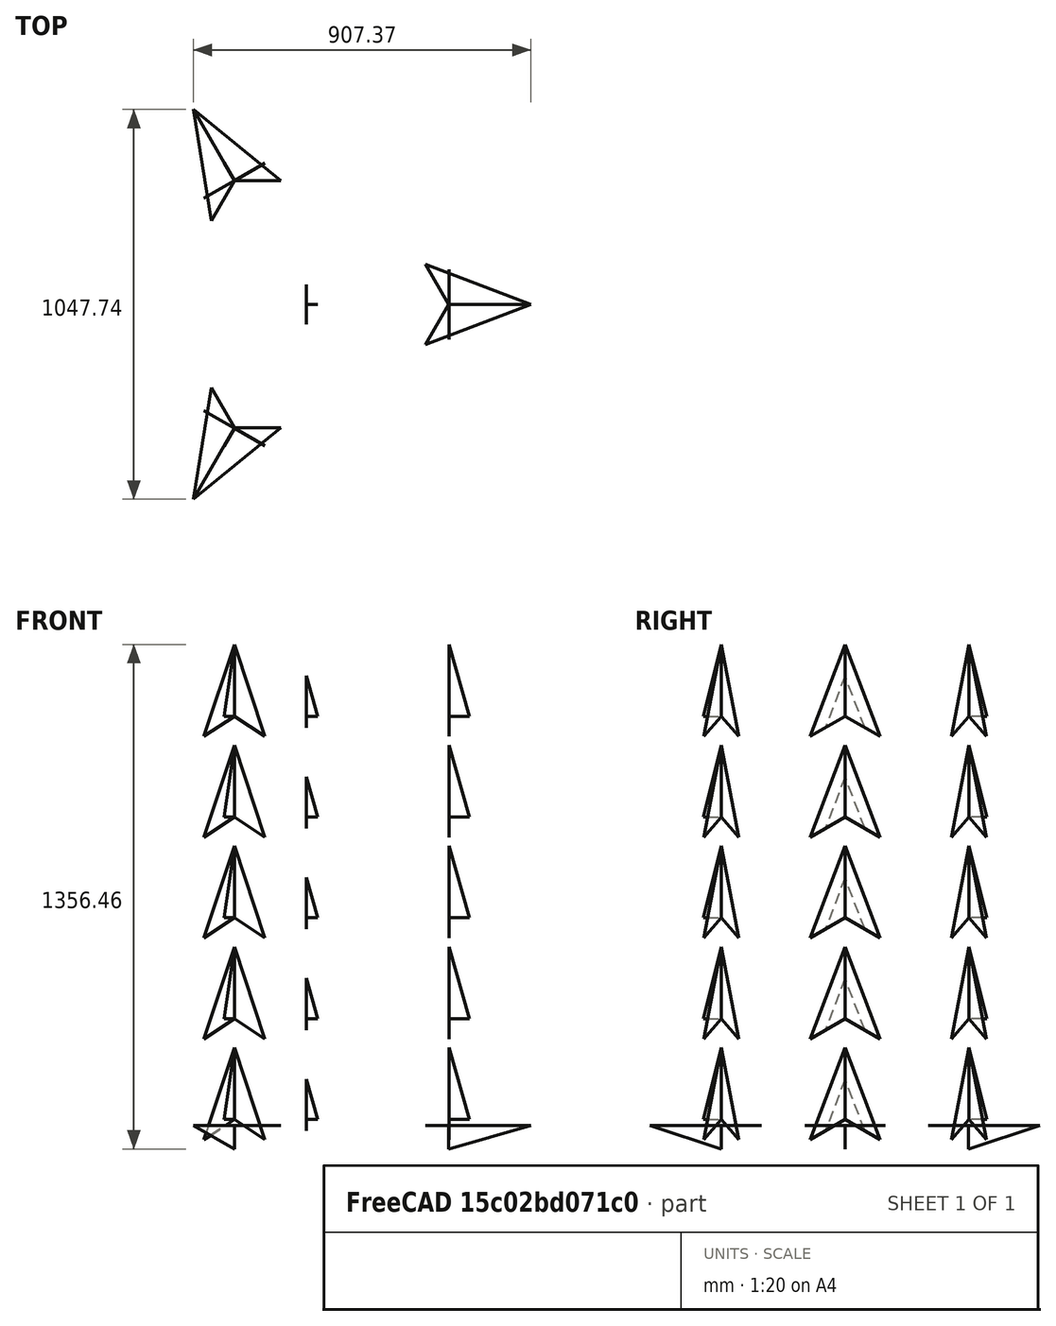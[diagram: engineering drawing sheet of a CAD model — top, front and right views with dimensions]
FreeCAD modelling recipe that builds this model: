
FCSTD DOCUMENT  (FreeCAD 1.1R38827 (Git))
Label: composit_stand3_plexiglass_outer_main
License: All rights reserved
LicenseURL: http://en.wikipedia.org/wiki/All_rights_reserved
objects: Part::FeaturePython×5, Sketcher::SketchObject×2, Part::Mirroring×2, App::Link×1, Part::Compound×1, Spreadsheet::Sheet×1
note: 12 computed .brp shape members not serialized (recipe doc carries the construction recipe); baked Part::Feature solids carry a one-line shape summary decoded from their .brp
EXTERNAL_REF file=composit_stand3_basement_bottom_main.FCStd obj=Placment
EXTERNAL_REF file=composit_stand3_bar_main.FCStd obj=Sketch

FEATURE [App::Link] Link  label="bar_placement"
  LinkTransform = true
  LinkedObject = -> <external composit_stand3_basement_bottom_main.FCStd>#Placment
FEATURE [Sketcher::SketchObject] Sketch001  label="base_Sketch_per"
  ArcFitTolerance = 0
  FullyConstrained = true
  MakeInternals = false
  expr: .Constraints.r = <<bar_placement>>.LinkedObject.Placement.Base.x
  expr: Constraints[2] = <<composit_stand3_bar_main>>#<<base_Sketch>>.Constraints.width - 8 mm
  sketch-geometry (1):
    g0: LineSegment StartX=383.5 StartY=-14.3 StartZ=0 EndX=383.5 EndY=14.3 EndZ=0
  constraints (3):
    c: Symmetric(g0,g0,g-1)
    c: DistanceX(g0) = 383.5  'r'
    c: DistanceY(g0,g0) = 28.6
FEATURE [Sketcher::SketchObject] Sketch  label="base_Sketch"
  ArcFitTolerance = 0
  ExternalGeometry = -> [Sketch001]
  FullyConstrained = false
  MakeInternals = false
  sketch-geometry (2):
    g0: ArcOfCircle CenterX=-17.9061 CenterY=-31.0143 CenterZ=0 NormalX=0 NormalY=0 NormalZ=1 AngleXU=0 Radius=403.956 StartAngle=0.112413 EndAngle=1.0472
    g1: LineSegment [constr] StartX=-17.9061 StartY=-31.0143 StartZ=0 EndX=184.072 EndY=318.822 EndZ=0
  constraints (6):
    c: Coincident(g1,g0)
    c: Coincident(g1,g0)
    c: Angle(g1) = 1.0472
    c: Coincident(g0,g-3)
    c: PointOnObject(g-1,g1)
    c: DistanceX(g-1,g-3) = 383.5  'offset'
FEATURE [Part::FeaturePython] PolarArray  # WARN: FeaturePython — macro-defined, semantics opaque (R4)
  Alignment = 0
  AttacherType = Attacher::AttachEngine3D
  CellStart = A1
  Count = 3
  DistributionLaw = 0
  EndInclusive = false
  ExposePlacement = false
  FlipX = false
  FlipZ = false
  GeneratorMode = 0
  MarkerShape = 1
  MarkerSize = 0
  NumElements = 3
  OrientMode = 2
  Radius = 383.5
  Reverse = false
  SpanEnd = 360
  SpanStart = 0
  Step = 120
  Type = lattice2PolarArray2.PolarArray
  UseArcRadius = false
  UseArcRange = 0
  VSGVersion = 1
  Values = 0.0 | 120.0 | 240.0
  ValuesSource = 2
  isLattice = 1
  expr: Radius = <<base_Sketch_per>>.Constraints.r
FEATURE [Part::FeaturePython] Populate  label="Populate PolarArray with base_Sketch_per"  # WARN: FeaturePython — macro-defined, semantics opaque (R4)
  Copying = 0
  ExposePlacement = false
  MarkerShape = 1
  MarkerSize = 0
  NumElements = 0
  Object = -> Sketch001
  OutputCompounding = 1
  PlacementsTo = -> PolarArray
  Referencing = 1
  Type = lattice2PopulateCopies.LatticePopulateCopies
  isLattice = 0
FEATURE [Part::Mirroring] Part__Mirroring  label="base_Sketch (Mirror #1)"
  Base = (0,0,0)
  Normal = (0.866025,-0.5,0)
  Source = -> Sketch
  expr: .Normal.x = sin(60)
  expr: .Normal.y = -cos(60)
FEATURE [Part::Compound] Compound
  Links = -> [Sketch,Part__Mirroring]
FEATURE [Part::Mirroring] Part__Mirroring001  label="Compound (Mirror #2)"
  Base = (0,0,0)
  Normal = (0,1,0)
  Source = -> Compound
FEATURE [Part::FeaturePython] Connect  # WARN: FeaturePython — macro-defined, semantics opaque (R4)
  Objects = -> [Compound,Part__Mirroring001,Populate]
  Tolerance = 0
FEATURE [Part::FeaturePython] LinearArray  label="bar_fix_placements"  # WARN: FeaturePython — macro-defined, semantics opaque (R4)
  Alignment = 0
  CellStart = A1
  Count = 5
  Dir = (1,0,0)
  DirIsDriven = true
  DistributionLaw = 0
  DrivenProperty = 1
  EndInclusive = true
  ExposePlacement = false
  GeneratorMode = 0
  MarkerShape = 1
  MarkerSize = 0
  NumElements = 5
  OrientMode = 1
  Placement = pos=(1,0,0) rot=(0,-1,0;1.5708rad)
  Point = (0,0,0)
  PointIsDriven = true
  Reverse = false
  SpanEnd = 1100
  SpanStart = 16
  Step = 271
  Type = lattice2LinearArray.LinearArray
  VSGVersion = 1
  Values = 16.0 | 287.0 | 558.0 | 829.0 | 1100.0
  ValuesSource = 2
  isLattice = 1
FEATURE [Spreadsheet::Sheet] Spreadsheet  label="Properties"
  cells = B2(height)==1210 mm; C2(thickness)==1.5 mm
FEATURE [Part::FeaturePython] Populate001  label="Populate PolarArray with bar_fix_placements"  # WARN: FeaturePython — macro-defined, semantics opaque (R4)
  Copying = 0
  ExposePlacement = false
  MarkerShape = 1
  MarkerSize = 0
  NumElements = 15
  Object = -> LinearArray
  OutputCompounding = 0
  PlacementsTo = -> PolarArray
  Referencing = 0
  Type = lattice2PopulateCopies.LatticePopulateCopies
  isLattice = 1
